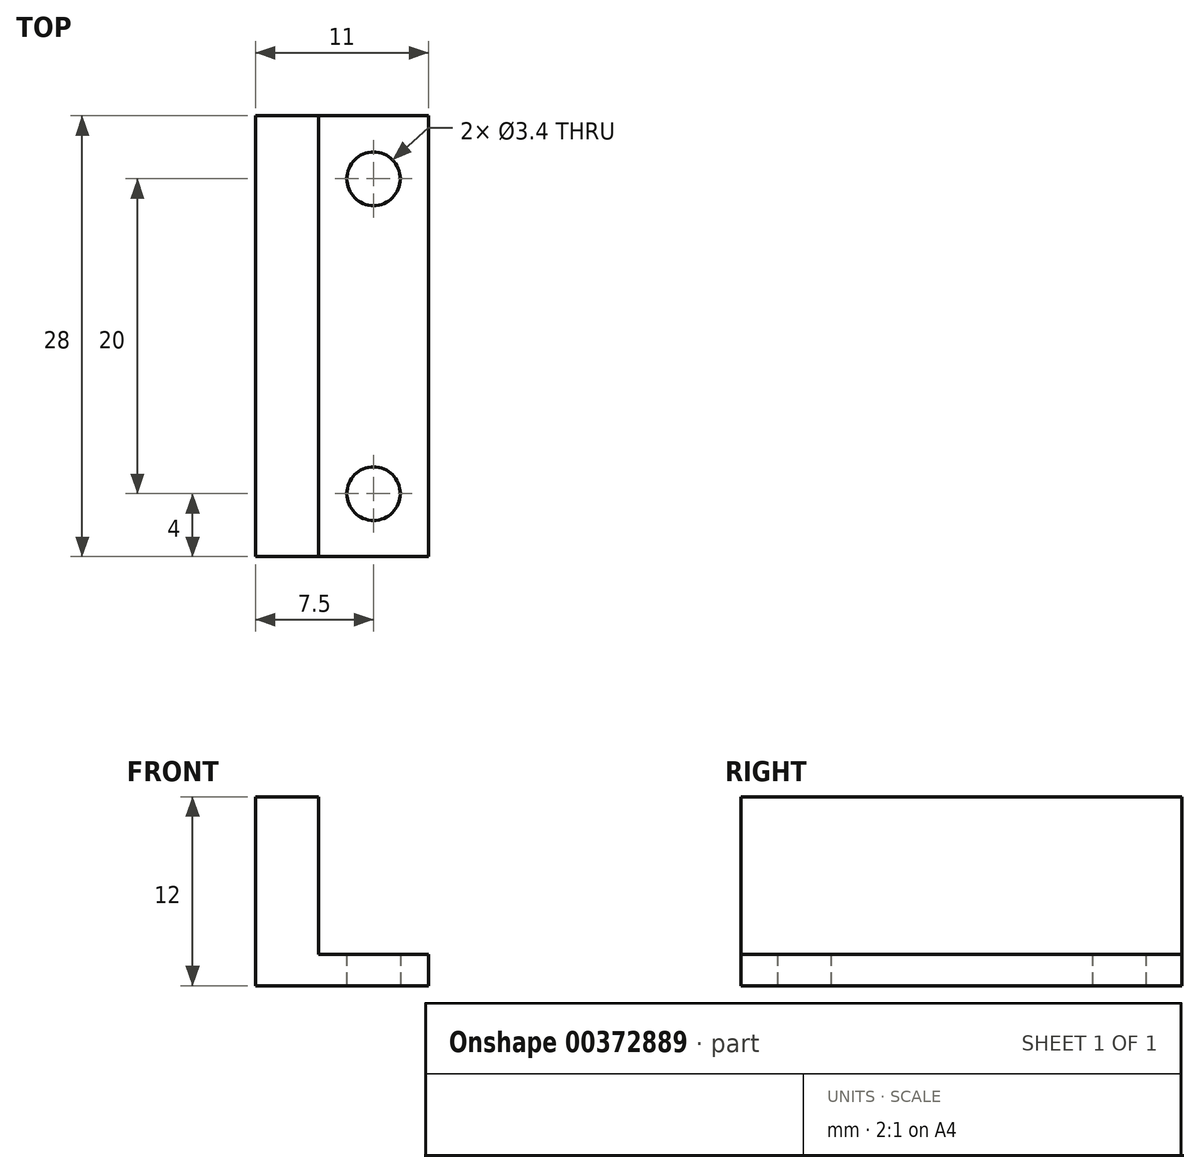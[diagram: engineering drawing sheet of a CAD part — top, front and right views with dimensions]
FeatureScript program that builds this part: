
annotation { "Feature Type Name" : "Feature", "Feature Type Description" : "" }
export const myFeature = defineFeature(function(context is Context, id is Id, definition is map)
    precondition{}
    {
        {
            var Q0;
            Q0=qCreatedBy(makeId("Front.planeOp"),FACE);
            var sketch = newSketch(context, id + "F0", { "sketchPlane" : qUnion([Q0])});
            skLineSegment(sketch, "E0", {"start": v(-5.5, 0) * mm, "end": v(5.5, 0) * mm});
            skLineSegment(sketch, "E1", {"start": v(5.5, 0) * mm, "end": v(5.5, 2) * mm});
            skLineSegment(sketch, "E2", {"start": v(-5.5, 12) * mm, "end": v(-5.5, 0) * mm});
            skLineSegment(sketch, "E3", {"start": v(-5.5, 12) * mm, "end": v(-1.5, 12) * mm});
            skLineSegment(sketch, "E4", {"start": v(-1.5, 12) * mm, "end": v(-1.5, 2) * mm});
            skLineSegment(sketch, "E5", {"start": v(-1.5, 2) * mm, "end": v(5.5, 2) * mm});
            skSolve(sketch);
        }
        {
            var Q0;
            Q0 = qSketchRegion(id + "F0", true);
            extrude(context, id + "F1", {"entities" : qUnion([Q0]), "endBound" : BoundingType.SYMMETRIC, "depth" : 28 * mm, "offsetDistance" : 25 * mm});
        }
        {
            var Q0;
            Q0=qCreatedBy(makeId("Top.planeOp"),FACE);
            var sketch = newSketch(context, id + "F2", { "sketchPlane" : qUnion([Q0])});
            skLineSegment(sketch, "E6", {"start": v(0, 0) * mm, "end": v(2, 0) * mm});
            skLineSegment(sketch, "E7", {"start": v(2, 10) * mm, "end": v(2, -10) * mm});
            skCircle(sketch, "E8", {"center": v(2, 10) * mm, "radius": 1.7 * mm});
            skCircle(sketch, "E9", {"center": v(2, -10) * mm, "radius": 1.7 * mm});
            skSolve(sketch);
        }
        {
            var Q0;
            Q0 = qSketchRegion(id + "F2", true);
            var Q1;
            Q1=makeQuery(id+"F1.opExtrude","SWEPT_FACE",FACE,{"disambiguationData":[OSD([sQuery(id+"F0.wireOp",EDGE,"E5")])]});
            extrude(context, id + "F3", {"entities" : qUnion([Q0]), "operationType" : NewBodyOperationType.REMOVE, "endBound" : BoundingType.UP_TO_SURFACE, "depth" : 25 * mm, "endBoundEntityFace" : qUnion([Q1]), "offsetDistance" : 25 * mm});
        }
    });
